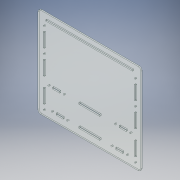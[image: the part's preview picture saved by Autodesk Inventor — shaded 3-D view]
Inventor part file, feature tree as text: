
AUTODESK INVENTOR PART (.ipt)
format: ipt  version: 2019 (Build 230136000, 136)  size: 241,664 bytes
history: native  units: mm
features: extrude x2, sketch x2, projected_geometry x1
ambient origin geometry x8: Origin, YZ Plane, XZ Plane, XY Plane, X Axis, Y Axis, Z Axis, Center Point
bodies: Solid1 (feature_tree)
feature tree (5):
  extrude  "Extrusion1"  Depth=3.5mm
  extrude  "Extrusion2"  Depth=250.0mm
  sketch  "Sketch1"  dims[d0=3.5mm d1=0.0mm d2=23.5mm]
  sketch  "Sketch2"  dims[d3=16.5mm d4=250.0mm d5=3.5mm d6=3.5mm d7=0.0mm]
  projected_geometry  "Projected Loop1"
